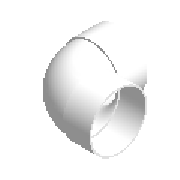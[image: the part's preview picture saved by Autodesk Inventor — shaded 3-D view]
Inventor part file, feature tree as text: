
AUTODESK INVENTOR PART (.ipt)
format: ipt  version: 2023.2 (Build 272271030, 271C)  size: 220,672 bytes
history: native  units: mm (DEFAULTED — no unit token found)
features: other x6, sketch x6, extrude x4, sweep x1
ambient origin geometry x8: Origin, YZ Plane, XZ Plane, XY Plane, X Axis, Y Axis, Z Axis, Center Point
bodies: Solid1 (feature_tree)
feature tree (17):
  sweep  "Sweep1"
  extrude  "Extrusion1"  Depth=17.4752mm
  extrude  "Extrusion2"  TaperAngle=0.0deg  [1 undecoded]
  extrude  "Extrusion3"  Depth=20.2438mm
  extrude  "Extrusion4"  Depth=18.1356mm
  other  "Work Axis1"
  other  "Work Point1"
  other  "Work Point2"
  other  "Work Axis2"
  other  "Work Point3"
  other  "Work Point4"
  sketch  "Sketch1"  dims[d0=30.1752mm d1=30.1752mm]
  sketch  "Sketch2"  dims[d2=17.4752mm d3=14.6812mm]
  sketch  "Sketch3"  dims[d4=21.59mm d5=0.0mm]
  sketch  "Sketch4"  dims[d6=27.0764mm d7=20.2438mm]
  sketch  "Sketch5"  dims[d8=0.0mm d9=18.1356mm]
  sketch  "Sketch6"  dims[d10=27.0764mm d11=18.1356mm d12=20.2438mm d13=0.0mm d14=21.5392mm d15=17.4752mm d16=-0.087207mm d17=21.5392mm d18=17.4752mm d19=-0.087207mm d33=0.0mm]
note: 1 required parameter value undecoded (feature->parameter linkage not recoverable at this tier; creation-order binding heuristic only, values carry confidence <= 0.55)
